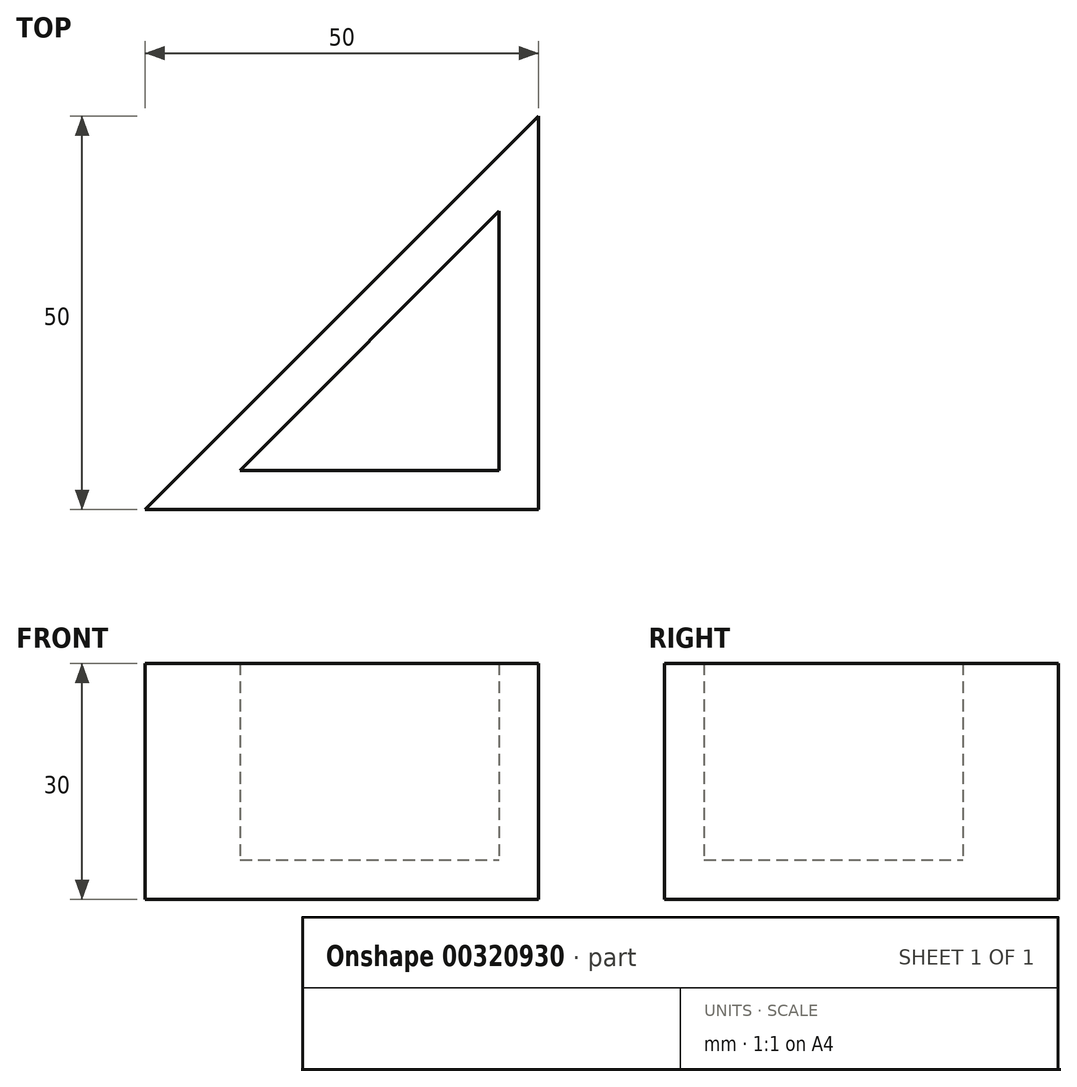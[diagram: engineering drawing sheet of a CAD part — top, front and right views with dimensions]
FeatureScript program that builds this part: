
annotation { "Feature Type Name" : "Feature", "Feature Type Description" : "" }
export const myFeature = defineFeature(function(context is Context, id is Id, definition is map)
    precondition{}
    {
        {
            var Q0;
            Q0=qCreatedBy(makeId("Top.planeOp"),FACE);
            var sketch = newSketch(context, id + "F0", { "sketchPlane" : qUnion([Q0])});
            skLineSegment(sketch, "E0", {"start": v(-50, 0) * mm, "end": v(0, 50) * mm});
            skLineSegment(sketch, "E1", {"start": v(-50, 0) * mm, "end": v(0, 0) * mm});
            skLineSegment(sketch, "E2", {"start": v(0, 0) * mm, "end": v(0, 50) * mm});
            skSolve(sketch);
        }
        {
            var Q0;
            Q0=makeQuery(id+"F0.imprint","IMPRINT",FACE,{"disambiguationData":[TD([[makeQuery(id+"F0.imprint","IMPRINT",EDGE,{"derivedFrom":sQuery(id+"F0.wireOp",EDGE,"E0")}),-1.0]])]});
            extrude(context, id + "F1", {"entities" : qUnion([Q0]), "depth" : 30 * mm});
        }
        {
            var Q0;
            Q0=makeQuery(id+"F1.opExtrude","CAP_FACE",FACE,{"disambiguationData":[OSD([sQuery(id+"F0.wireOp",EDGE,"E0"),sQuery(id+"F0.wireOp",EDGE,"E1"),sQuery(id+"F0.wireOp",EDGE,"E2")])],"isStart":false});
            shell(context, id + "F2", {"entities" : qUnion([Q0]), "thickness" : 5 * mm});
        }
    });
